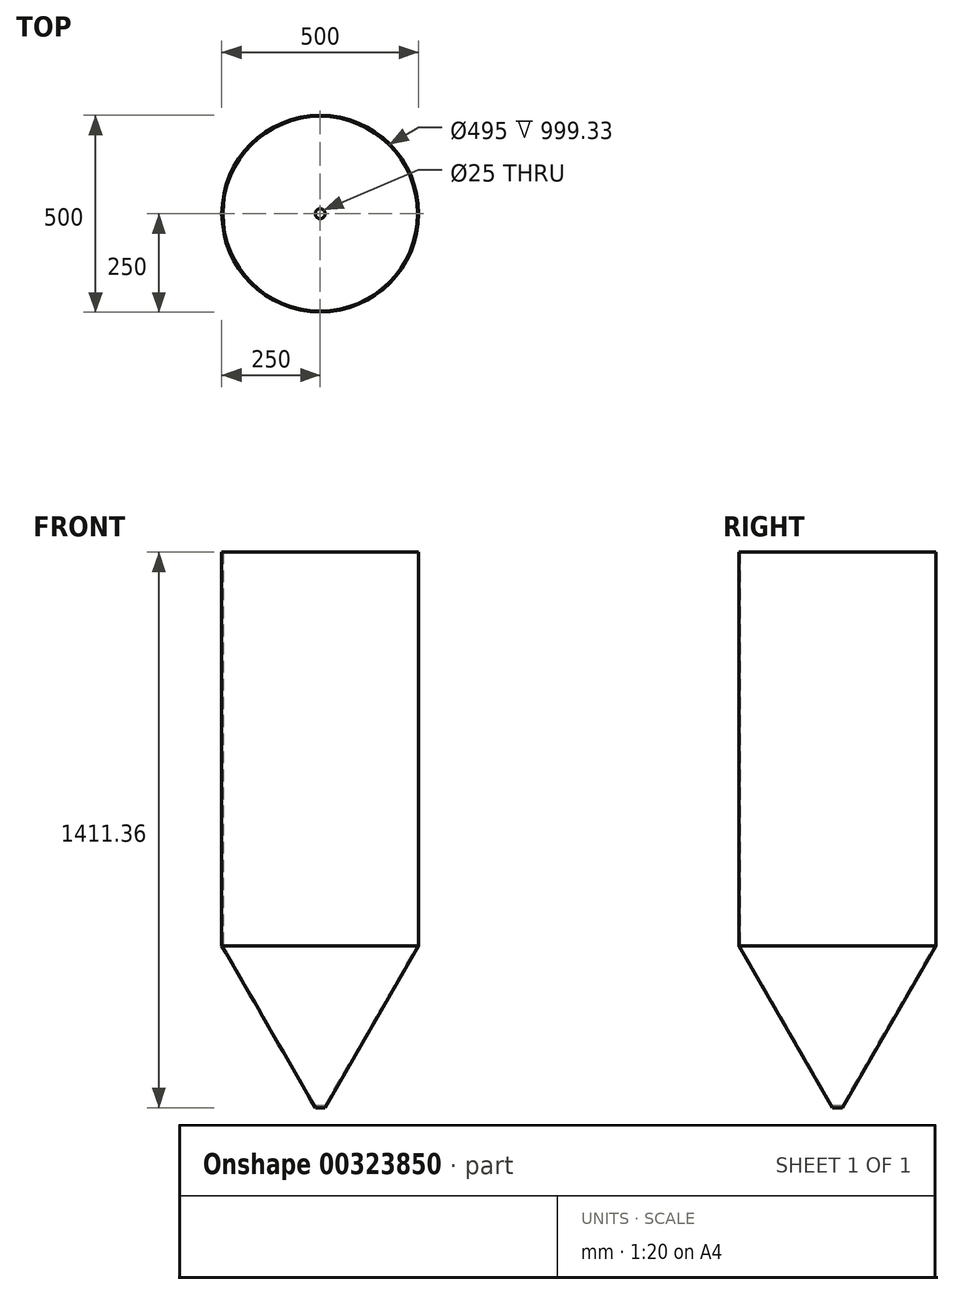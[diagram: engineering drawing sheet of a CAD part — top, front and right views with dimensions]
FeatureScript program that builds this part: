
annotation { "Feature Type Name" : "Feature", "Feature Type Description" : "" }
export const myFeature = defineFeature(function(context is Context, id is Id, definition is map)
    precondition{}
    {
        {
            var Q0;
            Q0=qCreatedBy(makeId("Top.planeOp"),FACE);
            var sketch = newSketch(context, id + "F0", { "sketchPlane" : qUnion([Q0])});
            skCircle(sketch, "E0", {"center": v(0, 0) * mm, "radius": 250 * mm});
            skSolve(sketch);
        }
        {
            var Q0;
            Q0 = qSketchRegion(id + "F0", true);
            extrude(context, id + "F1", {"entities" : qUnion([Q0]), "depth" : 1000 * mm});
        }
        {
            var Q0;
            Q0=makeQuery(id+"F1.opExtrude","CAP_FACE",FACE,{"disambiguationData":[OSD([sQuery(id+"F0.wireOp",EDGE,"E0")])],"isStart":true});
            var sketch = newSketch(context, id + "F2", { "sketchPlane" : qUnion([Q0])});
            skCircle(sketch, "E1.0", {"center": v(0, 0) * mm, "radius": 250 * mm});
            skSolve(sketch);
        }
        {
            var Q0;
            Q0 = qSketchRegion(id + "F2", true);
            extrude(context, id + "F3", {"entities" : qUnion([Q0]), "operationType" : NewBodyOperationType.ADD, "depth" : 500 * mm, "hasDraft" : true, "draftAngle" : 30 * degree, "draftPullDirection" : true});
        }
        {
            var Q0;
            Q0=makeQuery(id+"F1.opExtrude","CAP_FACE",FACE,{"disambiguationData":[OSD([sQuery(id+"F0.wireOp",EDGE,"E0")])],"isStart":false});
            shell(context, id + "F4", {"entities" : qUnion([Q0]), "thickness" : 2.5 * mm});
        }
        {
            var Q0;
            Q0=qCreatedBy(makeId("Top.planeOp"),FACE);
            var sketch = newSketch(context, id + "F5", { "sketchPlane" : qUnion([Q0])});
            skCircle(sketch, "E2", {"center": v(0, 0) * mm, "radius": 12.5 * mm});
            skSolve(sketch);
        }
        {
            var Q0;
            Q0 = qSketchRegion(id + "F5", true);
            extrude(context, id + "F6", {"entities" : qUnion([Q0]), "operationType" : NewBodyOperationType.REMOVE, "endBound" : BoundingType.THROUGH_ALL, "oppositeDirection" : true, "depth" : 25 * mm});
        }
    });
